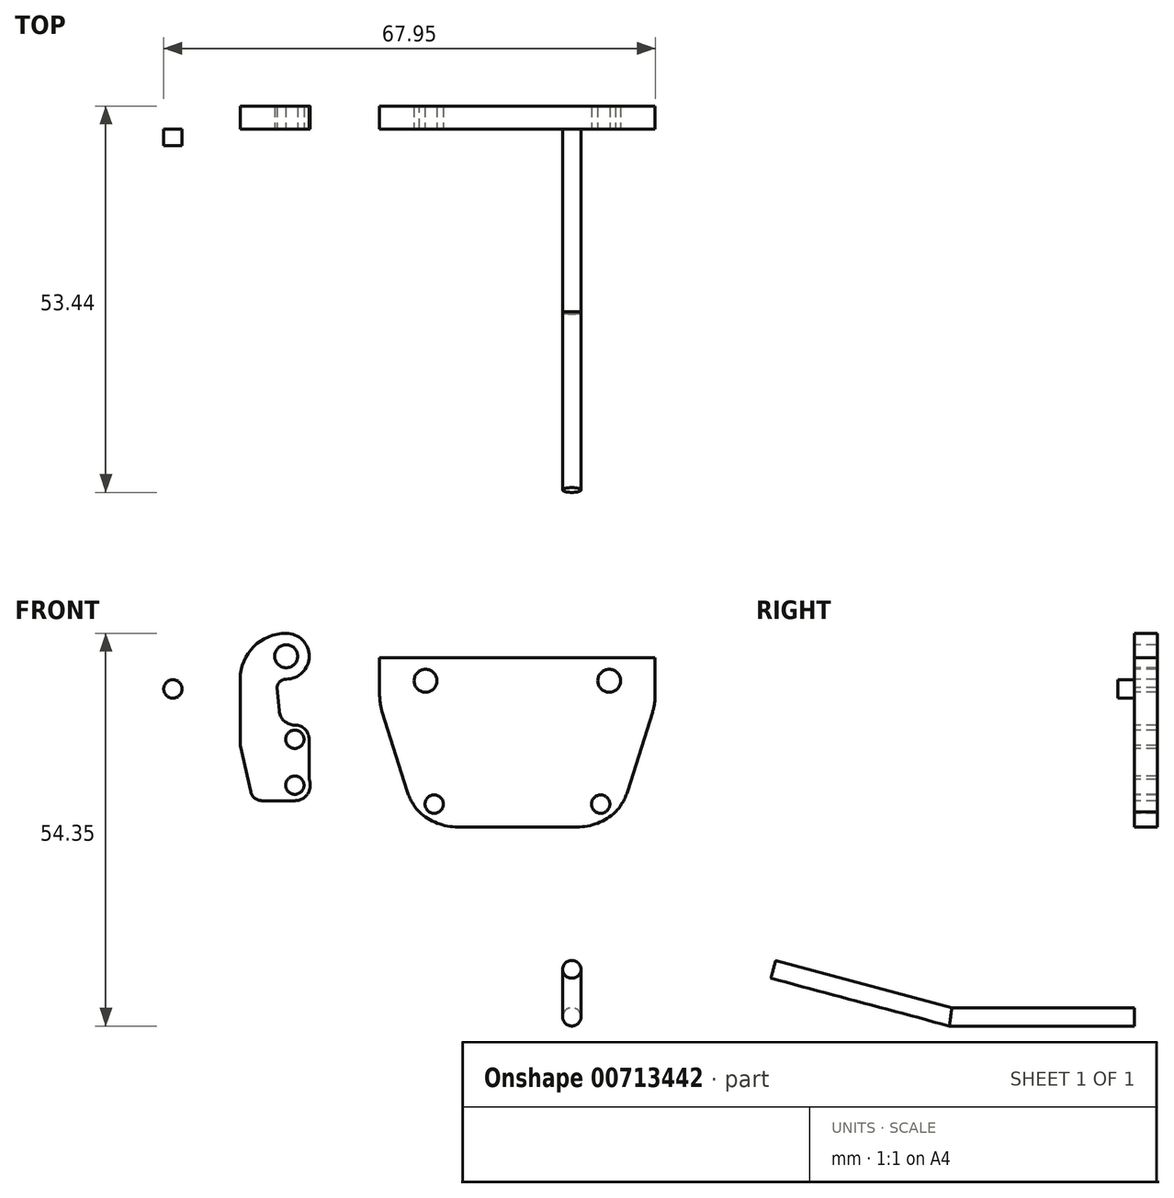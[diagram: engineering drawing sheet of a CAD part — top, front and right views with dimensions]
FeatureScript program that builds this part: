
annotation { "Feature Type Name" : "Feature", "Feature Type Description" : "" }
export const myFeature = defineFeature(function(context is Context, id is Id, definition is map)
    precondition{}
    {
        {
            var Q0;
            Q0=qCreatedBy(makeId("Front.planeOp"),FACE);
            var sketch = newSketch(context, id + "F0", { "sketchPlane" : qUnion([Q0])});
            skArc(sketch, "E0", {"start": v(-39.5, 46.73) * mm, "mid": v(-36.32, 49.9) * mm, "end": v(-39.5, 53.08) * mm});
            skLineSegment(sketch, "E1", {"start": v(-39.5, 46.73) * mm, "end": v(-39.5, 46.73) * mm});
            skLineSegment(sketch, "E2", {"start": v(-45.85, 46.73) * mm, "end": v(-45.85, 37.58) * mm});
            skPoint(sketch, "E3", {"position": v(-36.32, 49.9) * mm});
            skLineSegment(sketch, "E4", {"start": v(-42.86, 29.91) * mm, "end": v(-38.3, 29.91) * mm});
            skLineSegment(sketch, "E5", {"start": v(-36.32, 32.84) * mm, "end": v(-36.32, 38.4) * mm});
            skPoint(sketch, "E5.endSnap0", {"position": v(-45.85, 40.38) * mm});
            skPoint(sketch, "E6.endSnap0", {"position": v(-40.29, 29.91) * mm});
            skLineSegment(sketch, "E7", {"start": v(-40.47, 42.36) * mm, "end": v(-40.76, 45.56) * mm});
            skArc(sketch, "E8", {"start": v(-39.5, 46.73) * mm, "mid": v(-40.36, 46.4) * mm, "end": v(-40.76, 45.56) * mm});
            skPoint(sketch, "E9.end.orphan", {"position": v(-44.26, 48.99) * mm});
            skArc(sketch, "E10", {"start": v(-39.5, 53.08) * mm, "mid": v(-43.99, 51.22) * mm, "end": v(-45.85, 46.73) * mm});
            skArc(sketch, "E11", {"start": v(-40.47, 42.36) * mm, "mid": v(-39.77, 40.95) * mm, "end": v(-38.3, 40.38) * mm});
            skPoint(sketch, "E12", {"position": v(-36.32, 38.4) * mm});
            skArc(sketch, "E13", {"start": v(-36.32, 38.4) * mm, "mid": v(-36.9, 39.8) * mm, "end": v(-38.3, 40.38) * mm});
            skArc(sketch, "E14.MirrorCS", {"start": v(-36.32, 32.84) * mm, "mid": v(-36.54, 30.85) * mm, "end": v(-38.3, 29.91) * mm});
            skPoint(sketch, "E15.start.orphan", {"position": v(-36.32, 35.15) * mm});
            skPoint(sketch, "E16.orphan", {"position": v(-36.32, 29.91) * mm});
            skPoint(sketch, "E6.start.orphan", {"position": v(-36.32, 40.38) * mm});
            skPoint(sketch, "E17.orphan", {"position": v(-45.85, 34.03) * mm});
            skArc(sketch, "E18", {"start": v(-44.4, 31.15) * mm, "mid": v(-43.85, 30.26) * mm, "end": v(-42.86, 29.91) * mm});
            skLineSegment(sketch, "E19", {"start": v(-45.85, 37.58) * mm, "end": v(-44.4, 31.15) * mm});
            skPoint(sketch, "E20.orphan", {"position": v(-44.26, 29.91) * mm});
            skSolve(sketch);
        }
        {
            var Q0;
            Q0=makeQuery(id+"F0.imprint","IMPRINT",FACE,{"disambiguationData":[TD([[makeQuery(id+"F0.imprint","IMPRINT",EDGE,{"derivedFrom":sQuery(id+"F0.wireOp",EDGE,"E0")}),1.0]])]});
            extrude(context, id + "F1", {"entities" : qUnion([Q0]), "oppositeDirection" : true, "depth" : 3.17 * mm, "offsetDistance" : 25.4 * mm});
        }
        {
            var Q0;
            Q0=sQuery(id+"F0.wireOp",VERTEX,"E0.center");
            var Q1;
            Q1=makeQuery(id+"F1.opExtrude","SWEPT_BODY",BODY,{"disambiguationData":[OSD([sQuery(id+"F0.wireOp",EDGE,"E0"),sQuery(id+"F0.wireOp",EDGE,"E2"),sQuery(id+"F0.wireOp",EDGE,"E4"),sQuery(id+"F0.wireOp",EDGE,"E5"),sQuery(id+"F0.wireOp",EDGE,"E7"),sQuery(id+"F0.wireOp",EDGE,"E8"),sQuery(id+"F0.wireOp",EDGE,"E10"),sQuery(id+"F0.wireOp",EDGE,"E11"),sQuery(id+"F0.wireOp",EDGE,"E13"),sQuery(id+"F0.wireOp",EDGE,"E14.MirrorCS"),sQuery(id+"F0.wireOp",EDGE,"E18"),sQuery(id+"F0.wireOp",EDGE,"E19")])]});
            hole(context, id + "F2", {"style" : HoleStyle.SIMPLE, "endStyle" : HoleEndStyle.BLIND, "holeDiameter" : 3.17 * mm, "majorDiameter" : 6.35 * mm, "holeDepth" : 25.4 * mm, "isTappedThrough" : true, "tappedDepth" : 12.7 * mm, "tapClearance" : 3, "startFromSketch" : true, "locations" : qUnion([Q0]), "scope" : qUnion([Q1])});
        }
        {
            var Q0;
            Q0=sQuery(id+"F0.wireOp",VERTEX,"E13.center");
            var Q1;
            Q1=sQuery(id+"F0.wireOp",VERTEX,"E14.MirrorCS.center");
            var Q2;
            Q2=makeQuery(id+"F1.opExtrude","SWEPT_BODY",BODY,{"disambiguationData":[OSD([sQuery(id+"F0.wireOp",EDGE,"E0"),sQuery(id+"F0.wireOp",EDGE,"E2"),sQuery(id+"F0.wireOp",EDGE,"E4"),sQuery(id+"F0.wireOp",EDGE,"E5"),sQuery(id+"F0.wireOp",EDGE,"E7"),sQuery(id+"F0.wireOp",EDGE,"E8"),sQuery(id+"F0.wireOp",EDGE,"E10"),sQuery(id+"F0.wireOp",EDGE,"E11"),sQuery(id+"F0.wireOp",EDGE,"E13"),sQuery(id+"F0.wireOp",EDGE,"E14.MirrorCS"),sQuery(id+"F0.wireOp",EDGE,"E18"),sQuery(id+"F0.wireOp",EDGE,"E19")])]});
            hole(context, id + "F3", {"style" : HoleStyle.SIMPLE, "endStyle" : HoleEndStyle.BLIND, "holeDiameter" : 2.54 * mm, "majorDiameter" : 6.35 * mm, "holeDepth" : 25.4 * mm, "isTappedThrough" : true, "tappedDepth" : 12.7 * mm, "tapClearance" : 3, "startFromSketch" : true, "locations" : qUnion([Q0, Q1]), "scope" : qUnion([Q2])});
        }
        {
            var Q0;
            Q0=qCreatedBy(makeId("Front.planeOp"),FACE);
            var sketch = newSketch(context, id + "F4", { "sketchPlane" : qUnion([Q0])});
            skLineSegment(sketch, "E21.bottom", {"start": v(-26.57, 49.68) * mm, "end": v(11.53, 49.68) * mm});
            skLineSegment(sketch, "E21.left", {"start": v(-26.57, 49.68) * mm, "end": v(-26.57, 43.33) * mm});
            skLineSegment(sketch, "E21.right", {"start": v(11.53, 49.68) * mm, "end": v(11.53, 43.33) * mm});
            skLineSegment(sketch, "E22", {"start": v(-26.57, 46.5) * mm, "end": v(-20.22, 46.5) * mm});
            skLineSegment(sketch, "E23", {"start": v(11.53, 46.5) * mm, "end": v(5.18, 46.5) * mm});
            skPoint(sketch, "E24", {"position": v(-20.22, 46.5) * mm});
            skPoint(sketch, "E25", {"position": v(5.18, 46.5) * mm});
            skPoint(sketch, "E26", {"position": v(-19.03, 29.44) * mm});
            skPoint(sketch, "E27", {"position": v(3.99, 29.44) * mm});
            skLineSegment(sketch, "E28", {"start": v(-19.03, 26.27) * mm, "end": v(3.99, 26.27) * mm});
            skLineSegment(sketch, "E29", {"start": v(3.99, 26.27) * mm, "end": v(7.16, 29.44) * mm});
            skLineSegment(sketch, "E30", {"start": v(11.53, 43.33) * mm, "end": v(7.16, 29.44) * mm});
            skLineSegment(sketch, "E31", {"start": v(-19.03, 26.27) * mm, "end": v(-22.2, 29.44) * mm});
            skLineSegment(sketch, "E32", {"start": v(-26.57, 43.33) * mm, "end": v(-22.2, 29.44) * mm});
            skSolve(sketch);
        }
        {
            var Q0;
            {var subQ1=sQuery(id+"F4.wireOp",EDGE,"E21.bottom");Q0=makeQuery(id+"F4.imprint","IMPRINT",FACE,{"disambiguationData":[TD([[makeQuery(id+"F4.imprint","IMPRINT",EDGE,{"derivedFrom":subQ1}),-1.0]])]});}
            extrude(context, id + "F5", {"entities" : qUnion([Q0]), "oppositeDirection" : true, "depth" : 3.17 * mm, "offsetDistance" : 25.4 * mm});
        }
        {
            var Q0;
            Q0=sQuery(id+"F4.wireOp",VERTEX,"E24");
            var Q1;
            Q1=sQuery(id+"F4.wireOp",VERTEX,"E25");
            var Q2;
            Q2=makeQuery(id+"F5.opExtrude","SWEPT_BODY",BODY,{"disambiguationData":[OSD([sQuery(id+"F4.wireOp",EDGE,"E21.bottom"),sQuery(id+"F4.wireOp",EDGE,"E21.left"),sQuery(id+"F4.wireOp",EDGE,"E21.right"),sQuery(id+"F4.wireOp",EDGE,"E28"),sQuery(id+"F4.wireOp",EDGE,"E29"),sQuery(id+"F4.wireOp",EDGE,"E30"),sQuery(id+"F4.wireOp",EDGE,"E31"),sQuery(id+"F4.wireOp",EDGE,"E32")])]});
            hole(context, id + "F6", {"style" : HoleStyle.SIMPLE, "endStyle" : HoleEndStyle.BLIND, "holeDiameter" : 3.17 * mm, "majorDiameter" : 6.35 * mm, "holeDepth" : 25.4 * mm, "isTappedThrough" : true, "tappedDepth" : 12.7 * mm, "tapClearance" : 3, "startFromSketch" : true, "locations" : qUnion([Q0, Q1]), "scope" : qUnion([Q2])});
        }
        {
            var Q0;
            Q0=sQuery(id+"F4.wireOp",VERTEX,"E26");
            var Q1;
            Q1=sQuery(id+"F4.wireOp",VERTEX,"E27");
            var Q2;
            Q2=makeQuery(id+"F5.opExtrude","SWEPT_BODY",BODY,{"disambiguationData":[OSD([sQuery(id+"F4.wireOp",EDGE,"E21.bottom"),sQuery(id+"F4.wireOp",EDGE,"E21.left"),sQuery(id+"F4.wireOp",EDGE,"E21.right"),sQuery(id+"F4.wireOp",EDGE,"E28"),sQuery(id+"F4.wireOp",EDGE,"E29"),sQuery(id+"F4.wireOp",EDGE,"E30"),sQuery(id+"F4.wireOp",EDGE,"E31"),sQuery(id+"F4.wireOp",EDGE,"E32")])]});
            hole(context, id + "F7", {"style" : HoleStyle.SIMPLE, "endStyle" : HoleEndStyle.BLIND, "holeDiameter" : 2.54 * mm, "majorDiameter" : 6.35 * mm, "holeDepth" : 25.4 * mm, "isTappedThrough" : true, "tappedDepth" : 12.7 * mm, "tapClearance" : 3, "startFromSketch" : true, "locations" : qUnion([Q0, Q1]), "scope" : qUnion([Q2])});
        }
        {
            var Q0;
            Q0=makeQuery(id+"F5.opExtrude","SWEPT_EDGE",EDGE,{"disambiguationData":[OSD([sQuery(id+"F4.wireOp",EDGE,"E28"),sQuery(id+"F4.wireOp",EDGE,"E29")])]});
            var Q1;
            Q1=makeQuery(id+"F5.opExtrude","SWEPT_EDGE",EDGE,{"disambiguationData":[OSD([sQuery(id+"F4.wireOp",EDGE,"E29"),sQuery(id+"F4.wireOp",EDGE,"E30")])]});
            var Q2;
            Q2=makeQuery(id+"F5.opExtrude","SWEPT_EDGE",EDGE,{"disambiguationData":[OSD([sQuery(id+"F4.wireOp",EDGE,"E21.right"),sQuery(id+"F4.wireOp",EDGE,"E30")])]});
            var Q3;
            Q3=makeQuery(id+"F5.opExtrude","SWEPT_EDGE",EDGE,{"disambiguationData":[OSD([sQuery(id+"F4.wireOp",EDGE,"E21.left"),sQuery(id+"F4.wireOp",EDGE,"E32")])]});
            var Q4;
            Q4=makeQuery(id+"F5.opExtrude","SWEPT_EDGE",EDGE,{"disambiguationData":[OSD([sQuery(id+"F4.wireOp",EDGE,"E31"),sQuery(id+"F4.wireOp",EDGE,"E32")])]});
            var Q5;
            Q5=makeQuery(id+"F5.opExtrude","SWEPT_EDGE",EDGE,{"disambiguationData":[OSD([sQuery(id+"F4.wireOp",EDGE,"E28"),sQuery(id+"F4.wireOp",EDGE,"E31")])]});
            fillet(context, id + "F8", {"entities" : qUnion([Q0, Q1, Q2, Q3, Q4, Q5]), "radius" : 7.94 * mm, "tangentPropagation" : true, "allowEdgeOverflow" : false});
        }
        {
            var Q0;
            Q0=qCreatedBy(makeId("Front.planeOp"),FACE);
            var sketch = newSketch(context, id + "F9", { "sketchPlane" : qUnion([Q0])});
            skCircle(sketch, "E33", {"center": v(-55.15, 45.37) * mm, "radius": 1.27 * mm});
            skSolve(sketch);
        }
        {
            var Q0;
            Q0=makeQuery(id+"F9.imprint","IMPRINT",FACE,{"disambiguationData":[TD([[makeQuery(id+"F9.imprint","IMPRINT",EDGE,{"derivedFrom":sQuery(id+"F9.wireOp",EDGE,"E33")}),1.0]])]});
            extrude(context, id + "F10", {"entities" : qUnion([Q0]), "depth" : 2.3 * mm, "offsetDistance" : 25.4 * mm});
        }
        {
            var Q0;
            Q0=qCreatedBy(makeId("Front.planeOp"),FACE);
            var sketch = newSketch(context, id + "F11", { "sketchPlane" : qUnion([Q0])});
            skCircle(sketch, "E34", {"center": v(0, 0) * mm, "radius": 1.27 * mm});
            skSolve(sketch);
        }
        {
            var Q0;
            Q0=qCreatedBy(makeId("Right.planeOp"),FACE);
            var sketch = newSketch(context, id + "F12", { "sketchPlane" : qUnion([Q0])});
            skLineSegment(sketch, "E35", {"start": v(0, 0) * mm, "end": v(-25.4, 0) * mm});
            skLineSegment(sketch, "E36", {"start": v(-25.4, 0) * mm, "end": v(-49.93, 6.57) * mm});
            skSolve(sketch);
        }
        {
            var Q0;
            Q0=makeQuery(id+"F11.imprint","IMPRINT",FACE,{"disambiguationData":[TD([[makeQuery(id+"F11.imprint","IMPRINT",EDGE,{"derivedFrom":sQuery(id+"F11.wireOp",EDGE,"E34")}),1.0]])]});
            var Q1;
            Q1=sQuery(id+"F12.wireOp",EDGE,"E35");
            var Q2;
            Q2=sQuery(id+"F12.wireOp",EDGE,"E36");
            sweep(context, id + "F13", {"profiles" : qUnion([Q0]), "path" : qUnion([Q1, Q2])});
        }
    });
